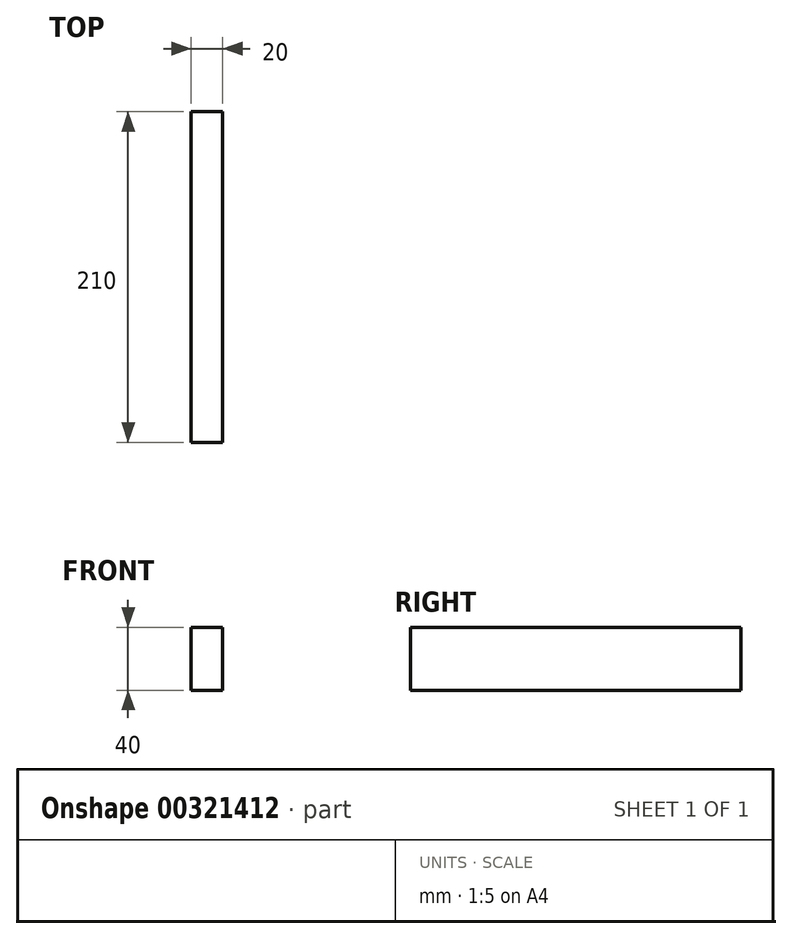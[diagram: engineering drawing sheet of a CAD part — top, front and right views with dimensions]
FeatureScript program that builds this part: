
annotation { "Feature Type Name" : "Feature", "Feature Type Description" : "" }
export const myFeature = defineFeature(function(context is Context, id is Id, definition is map)
    precondition{}
    {
        {
            var Q0;
            Q0=qCreatedBy(makeId("Front.planeOp"),FACE);
            var sketch = newSketch(context, id + "F0", { "sketchPlane" : qUnion([Q0])});
            skLineSegment(sketch, "E0.bottom", {"start": v(10, -20) * mm, "end": v(-10, -20) * mm});
            skLineSegment(sketch, "E0.top", {"start": v(10, 20) * mm, "end": v(-10, 20) * mm});
            skLineSegment(sketch, "E0.left", {"start": v(10, -20) * mm, "end": v(10, 20) * mm});
            skLineSegment(sketch, "E0.right", {"start": v(-10, -20) * mm, "end": v(-10, 20) * mm});
            skPoint(sketch, "E0.middle", {"position": v(0, 0) * mm});
            skSolve(sketch);
        }
        {
            var Q0;
            Q0=makeQuery(id+"F0.imprint","IMPRINT",FACE,{"disambiguationData":[TD([[makeQuery(id+"F0.imprint","IMPRINT",EDGE,{"derivedFrom":sQuery(id+"F0.wireOp",EDGE,"E0.bottom")}),-1.0]])]});
            extrude(context, id + "F1", {"entities" : qUnion([Q0]), "depth" : 210 * mm});
        }
    });
